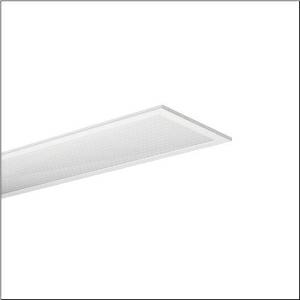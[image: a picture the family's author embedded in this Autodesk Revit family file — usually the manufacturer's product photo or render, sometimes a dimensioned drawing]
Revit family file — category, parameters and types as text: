
# Revit family: apollon_21_linear_51mq14wd2t12
name_source: partatom
category: Lighting Fixtures
units: mm (PartAtom-declared; Revit-internal decimal feet)

## family parameters
Cut with Voids When Loaded = No
Host = Face
Light Source = No
Part Type = Normal
Room Calculation Point = No
Round Connector Dimension = Use Diameter
Shared = No

## types (1)
- --- (1 x LED 2700 K ... 6500 K, 4200 lm, 44 W, 6500K)
    Apparent Load = 44 VA
    CIE Flux Codes = 60 87 97 100 100
    Color Rendering = 80
    Color Temperature = 6500K
    Default Elevation = 1800 mm
    Description = Apollon 21 linear, office luminaire, primary optical cover: micro prismatic cover, of PMMA, CAT 2 (L<= 3000cd/m²), light emission: direct distribution, primary light characteristic: symmetric, installation type: lay-in mounting, recessed, LED, rated luminous flux: 4.200lm, luminous efficacy: 96lm/W, light colour: 8tw, colour temperature: 2700..6500K, control gear: DALI DT8, with terminal, 5-pole, mains connection: 220..240V, AC, 50/60Hz, rated input power: 44W, housing, of aluminium, coated, traffic white (RAL 9016), module: M625, length: 1.245mm, width: 307mm, height: 30mm, housing upper side, of sheet steel, galvanised, protection rating (complete): IP20, protection rating (lamp compartment, on room side): IP50, insulation class (complete): insulation class I (protective earthing), certification: CE, ENEC, packaging unit: 1 piece
    Height = 0 mm  [stored 0 ft]
    Lamp = 1 x LED 2700 K ... 6500 K
    Lamp Light Flux = 4200 lm
    Lamp Power = 44 W
    Lamp count = 1
    Length = 1245 mm
    Luminous efficacy = 95 lm/W
    Manufacturer = Siteco
    ModVariant = No
    Model = 51MQ14WD2T12
    Mounting Place = Ceiling
    Mounting Type = Recessed
    Number of Poles = 1
    OnlyDefault = Yes
    Power Factor = 1
    Product Name = Apollon 21 linear
    Product group = office luminaire | ceiling recessed
    ProductGroupID = 400
    Protection Class = Protection class I
    Protection Degree = IP 20
    RLX_Detail_Level = 1
    RLX_Emergency_Light_Flux = 0 lm
    RLX_Emergency_Type = 0
    RLX_Emergency_Type_DB = No
    RlxData = <blob elided: 17609 chars, md5=9717e9ca>
    Socket = socket
    Standby Power = 0 W
    System Light Flux = 4200 lm
    System Power = 44 W
    Type Comments = individual setting: CCT=6500K, colour temperature 6500K
    Type Image = l_1291045.jpg
    URL = http://relux.com
    VarID = @adj_194979
    Voltage = 0 V
    Weight = 0.00 kg
    Width = 307 mm

note: [stored X ft] marks values corroborated as IEEE doubles in the binary element streams (Revit-internal decimal feet)

## geometry (parser evidence)
native form markers: Blend x4, Sweep x11
no freeform markers — native parametric forms only
